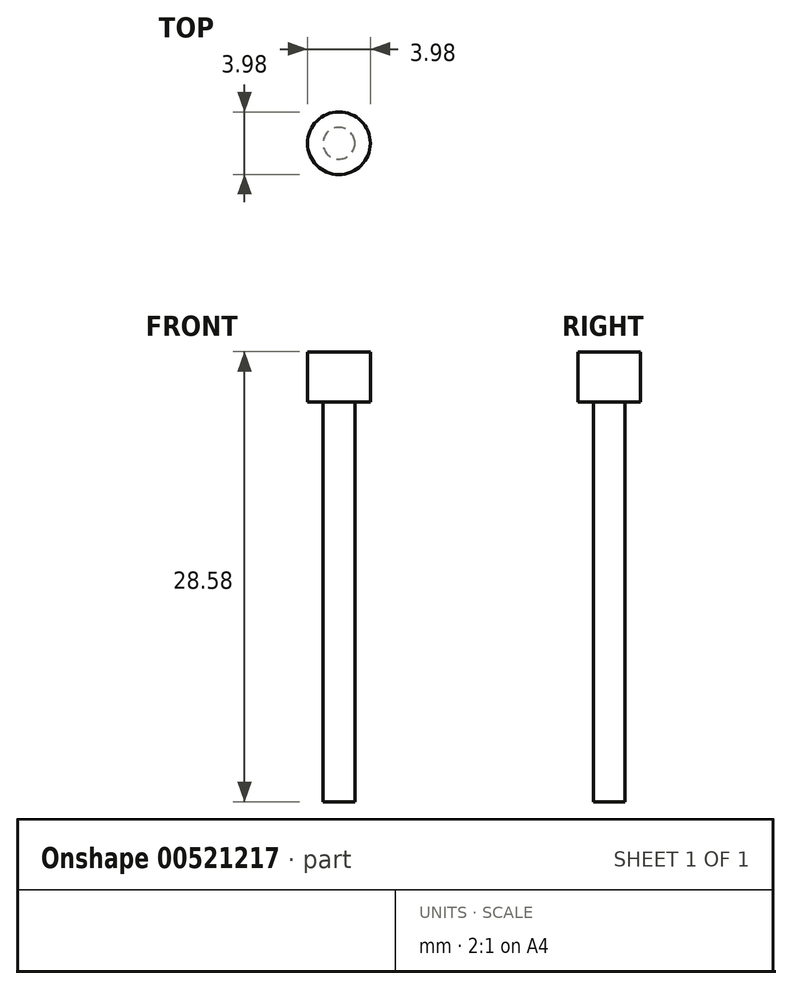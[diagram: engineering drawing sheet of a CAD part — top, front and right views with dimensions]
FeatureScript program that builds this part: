
annotation { "Feature Type Name" : "Feature", "Feature Type Description" : "" }
export const myFeature = defineFeature(function(context is Context, id is Id, definition is map)
    precondition{}
    {
        {
            var Q0;
            Q0=qCreatedBy(makeId("Top.planeOp"),FACE);
            var sketch = newSketch(context, id + "F0", { "sketchPlane" : qUnion([Q0])});
            skCircle(sketch, "E0", {"center": v(0, 0) * mm, "radius": 1.01 * mm});
            skSolve(sketch);
        }
        {
            var Q0;
            Q0=qSketchRegion(id+"F0",true);
            extrude(context, id + "F1", {"entities" : qUnion([Q0]), "oppositeDirection" : true, "depth" : 25.4 * mm, "offsetDistance" : 25.4 * mm});
        }
        {
            var Q0;
            Q0=qCreatedBy(makeId("Top.planeOp"),FACE);
            var sketch = newSketch(context, id + "F2", { "sketchPlane" : qUnion([Q0])});
            skCircle(sketch, "E1", {"center": v(0, 0) * mm, "radius": 2 * mm});
            skSolve(sketch);
        }
        {
            var Q0;
            Q0=qSketchRegion(id+"F2",true);
            extrude(context, id + "F3", {"entities" : qUnion([Q0]), "operationType" : NewBodyOperationType.ADD, "depth" : 3.17 * mm, "offsetDistance" : 25.4 * mm});
        }
    });
